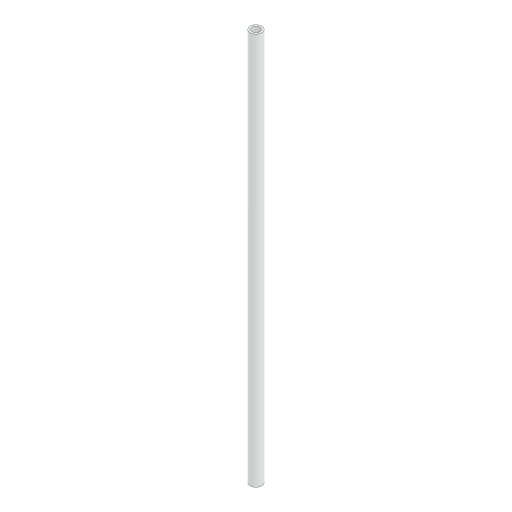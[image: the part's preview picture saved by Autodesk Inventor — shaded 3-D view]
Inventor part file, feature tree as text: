
AUTODESK INVENTOR PART (.ipt)
format: ipt  version: 2024.3 (Build 283343000, 343)  size: 240,640 bytes
history: native  units: mm
features: extrude x1, sketch x1
ambient origin geometry x8: Origin, YZ Plane, XZ Plane, XY Plane, X Axis, Y Axis, Z Axis, Center Point
bodies: Solid1 (feature_tree)
feature tree (2):
  extrude  "Extrusion1"  Depth=100.0mm
  sketch  "Sketch1"  dims[d0=3.0mm d1=2.0mm d2=100.0mm d3=0.0mm]
